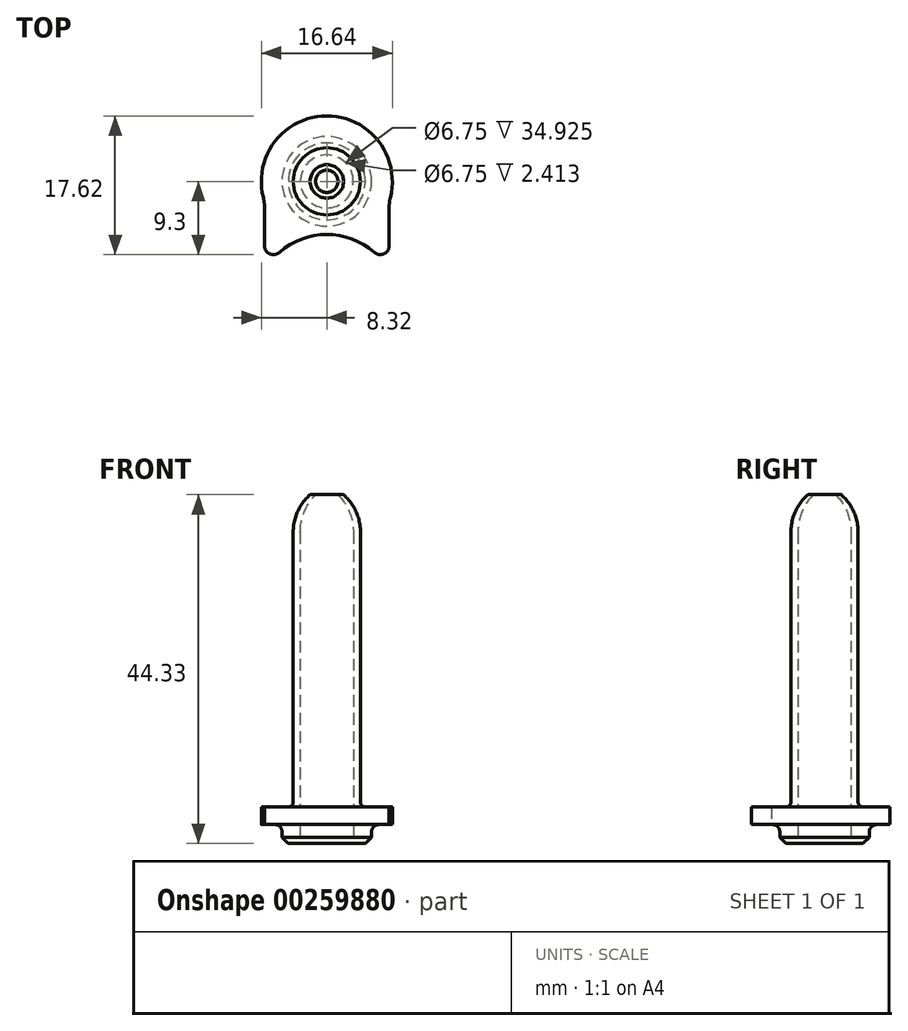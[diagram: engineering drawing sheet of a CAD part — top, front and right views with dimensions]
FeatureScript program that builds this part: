
annotation { "Feature Type Name" : "Feature", "Feature Type Description" : "" }
export const myFeature = defineFeature(function(context is Context, id is Id, definition is map)
    precondition{}
    {
        {
            var Q0;
            Q0=qCreatedBy(makeId("Right.planeOp"),FACE);
            var sketch = newSketch(context, id + "F0", { "sketchPlane" : qUnion([Q0])});
            skLineSegment(sketch, "E0.top", {"start": v(3.37, -1.2) * mm, "end": v(5.69, -1.2) * mm});
            skLineSegment(sketch, "E0.right", {"start": v(5.69, 0.32) * mm, "end": v(5.69, -1.2) * mm});
            skPoint(sketch, "E0.middle", {"position": v(0, 0) * mm});
            skPoint(sketch, "E1.middle", {"position": v(0, 2.32) * mm});
            skPoint(sketch, "E1.middle.positionSnap0", {"position": v(0, 1.2) * mm});
            skPoint(sketch, "E1.centerSnap0", {"position": v(0, 1.2) * mm});
            skLineSegment(sketch, "E2.left", {"start": v(4.27, 4.08) * mm, "end": v(4.27, 38.37) * mm});
            skPoint(sketch, "E2.middle", {"position": v(0, 23.28) * mm});
            skLineSegment(sketch, "E3.bottom", {"start": v(1.42, 43.12) * mm, "end": v(2.13, 43.12) * mm});
            skLineSegment(sketch, "E3.right", {"start": v(3.37, 38.37) * mm, "end": v(3.37, -1.2) * mm});
            skLineSegment(sketch, "E4.trimOffspring", {"start": v(2.13, 43.12) * mm, "end": v(1.42, 43.12) * mm});
            skPoint(sketch, "E5.orphan", {"position": v(4.27, 43.12) * mm});
            skArc(sketch, "E6.trimOffspring", {"start": v(4.27, 38.37) * mm, "mid": v(3.7, 40.97) * mm, "end": v(2.13, 43.12) * mm});
            skArc(sketch, "E7.trimOffspring", {"start": v(3.37, 38.37) * mm, "mid": v(2.87, 40.93) * mm, "end": v(1.42, 43.12) * mm});
            skPoint(sketch, "E8.center.orphan", {"position": v(2.08, 38.37) * mm});
            skPoint(sketch, "E9.trimOffspring.end.orphan", {"position": v(-4.27, 43.12) * mm});
            skLineSegment(sketch, "E10", {"start": v(0, -1.2) * mm, "end": v(0, 43.12) * mm});
            skPoint(sketch, "E1.left.end.orphan", {"position": v(-8.32, 3.44) * mm});
            skPoint(sketch, "E11.orphan", {"position": v(-8.32, 1.2) * mm});
            skPoint(sketch, "E0.left.end.orphan", {"position": v(-5.69, -1.2) * mm});
            skPoint(sketch, "E0.left.start.orphan", {"position": v(-5.69, 1.2) * mm});
            skLineSegment(sketch, "E12.trimOffspring", {"start": v(6.58, 1.2) * mm, "end": v(7.65, 1.2) * mm});
            skLineSegment(sketch, "E13.trimOffspring", {"start": v(4.9, 3.44) * mm, "end": v(7.65, 3.44) * mm});
            skPoint(sketch, "E14.trimOffspring.end.orphan", {"position": v(-4.27, 3.44) * mm});
            skPoint(sketch, "E15.visualSharp", {"position": v(4.27, 3.44) * mm});
            skArc(sketch, "E15.filletArc", {"start": v(4.27, 4.08) * mm, "mid": v(4.45, 3.63) * mm, "end": v(4.9, 3.44) * mm});
            skPoint(sketch, "E16.visualSharp", {"position": v(5.69, 1.2) * mm});
            skArc(sketch, "E16.filletArc", {"start": v(6.58, 1.2) * mm, "mid": v(5.95, 0.95) * mm, "end": v(5.69, 0.32) * mm});
            skPoint(sketch, "E17.trimOffspring.end.orphan", {"position": v(-2.13, 43.12) * mm});
            skArc(sketch, "E18", {"start": v(7.65, 1.2) * mm, "mid": v(8.32, 2.32) * mm, "end": v(7.65, 3.44) * mm});
            skPoint(sketch, "E19.orphan", {"position": v(8.32, 3.44) * mm});
            skPoint(sketch, "E20.orphan", {"position": v(8.32, 1.2) * mm});
            skSolve(sketch);
        }
        {
            var Q0;
            Q0 = qSketchRegion(id + "F0", true);
            var Q1;
            Q1=sQuery(id+"F0.wireOp",EDGE,"E10");
            revolve(context, id + "F1", {"entities" : qUnion([Q0]), "axis" : qUnion([Q1]), "revolveType" : RevolveType.FULL});
        }
        {
            var Q0;
            Q0=makeQuery(id+"F1.opRevolve","SWEPT_EDGE",EDGE,{"disambiguationData":[OSD([sQuery(id+"F0.wireOp",EDGE,"E0.top"),sQuery(id+"F0.wireOp",EDGE,"E0.right")])]});
            chamfer(context, id + "F2", {"entities" : qUnion([Q0]), "chamferType" : ChamferType.OFFSET_ANGLE, "width" : 0.8 * mm, "oppositeDirection" : false, "angle" : 45 * degree, "tangentPropagation" : true});
        }
        {
            var Q0;
            Q0=makeQuery(id+"F1.opRevolve","SWEPT_FACE",FACE,{"disambiguationData":[OSD([sQuery(id+"F0.wireOp",EDGE,"E12.trimOffspring")])]});
            var sketch = newSketch(context, id + "F3", { "sketchPlane" : qUnion([Q0])});
            skArc(sketch, "E21", {"start": v(-8.07, 2.03) * mm, "mid": v(-7.96, 2.6) * mm, "end": v(-7.92, 3.19) * mm});
            skArc(sketch, "E22", {"start": v(-6.03, 9.02) * mm, "mid": v(-7.25, 9.2) * mm, "end": v(-7.92, 8.16) * mm});
            skArc(sketch, "E23", {"start": v(-6.03, 9.02) * mm, "mid": v(0, 6.75) * mm, "end": v(6.03, 9.02) * mm});
            skArc(sketch, "E24.MirrorC", {"start": v(6.03, 9.02) * mm, "mid": v(7.25, 9.2) * mm, "end": v(7.92, 8.16) * mm});
            skLineSegment(sketch, "E25", {"start": v(-7.92, 8.16) * mm, "end": v(-7.92, 3.19) * mm});
            skLineSegment(sketch, "E26", {"start": v(7.92, 8.16) * mm, "end": v(7.92, 3.19) * mm});
            skArc(sketch, "E27.MirrorCS", {"start": v(8.07, 2.03) * mm, "mid": v(7.96, 2.6) * mm, "end": v(7.92, 3.19) * mm});
            skArc(sketch, "E28", {"start": v(3.61, 7.5) * mm, "mid": v(0, 8.32) * mm, "end": v(-3.61, 7.5) * mm});
            skPoint(sketch, "E29.bottom.start.orphan", {"position": v(-8.32, 0) * mm});
            skArc(sketch, "E30", {"start": v(-8.07, 2.03) * mm, "mid": v(0, -8.32) * mm, "end": v(8.07, 2.03) * mm});
            skSolve(sketch);
        }
        {
            var Q0;
            {var subQ1=sQuery(id+"F0.wireOp",EDGE,"E12.trimOffspring");Q0=makeQuery(id+"F3.imprint","IMPRINT",FACE,{"disambiguationData":[TD([[makeQuery(id+"F3.imprint","IMPRINT",EDGE,{"derivedFrom":makeQuery(id+"F1.opRevolve","SWEPT_EDGE",EDGE,{"disambiguationData":[OSD([subQ1,sQuery(id+"F0.wireOp",EDGE,"E16.filletArc")])]})}),-1.0]])]});}
            var sketch = newSketch(context, id + "F4", { "sketchPlane" : qUnion([Q0])});
            skArc(sketch, "E31", {"start": v(-3.61, 7.5) * mm, "mid": v(0, 6.75) * mm, "end": v(3.61, 7.5) * mm});
            skArc(sketch, "E32", {"start": v(3.61, 7.5) * mm, "mid": v(0, 8.32) * mm, "end": v(-3.61, 7.5) * mm});
            skPoint(sketch, "E33.bottom.start.orphan", {"position": v(-8.32, 0) * mm});
            skPoint(sketch, "E34.start.orphan", {"position": v(7.92, 8.16) * mm});
            skPoint(sketch, "E35.center.orphan", {"position": v(-6.78, 8.16) * mm});
            skPoint(sketch, "E36.start.orphan", {"position": v(-7.92, 8.16) * mm});
            skSolve(sketch);
        }
        {
            var Q0;
            Q0 = qSketchRegion(id + "F3", true);
            extrude(context, id + "F5", {"entities" : qUnion([Q0]), "operationType" : NewBodyOperationType.ADD, "oppositeDirection" : true, "depth" : 2.24 * mm});
        }
        {
            var Q0;
            Q0 = qSketchRegion(id + "F4", true);
            extrude(context, id + "F6", {"entities" : qUnion([Q0]), "operationType" : NewBodyOperationType.REMOVE, "oppositeDirection" : true, "depth" : 25.4 * mm});
        }
    });
